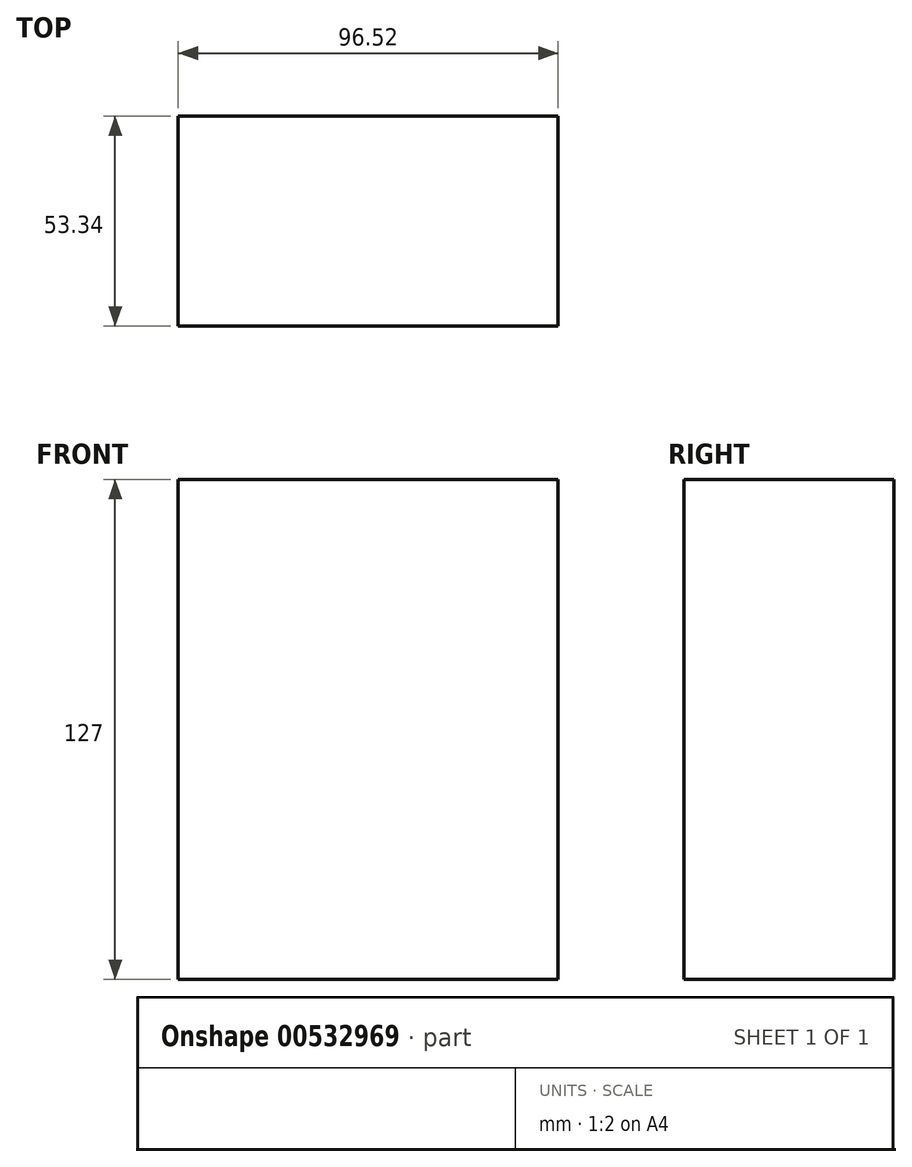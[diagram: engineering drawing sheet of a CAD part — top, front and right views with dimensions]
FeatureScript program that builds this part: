
annotation { "Feature Type Name" : "Feature", "Feature Type Description" : "" }
export const myFeature = defineFeature(function(context is Context, id is Id, definition is map)
    precondition{}
    {
        {
            var Q0;
            Q0=qCreatedBy(makeId("Front.planeOp"),FACE);
            var sketch = newSketch(context, id + "F0", { "sketchPlane" : qUnion([Q0])});
            skLineSegment(sketch, "E0.bottom", {"start": v(48.26, 63.5) * mm, "end": v(-48.26, 63.5) * mm});
            skLineSegment(sketch, "E0.top", {"start": v(48.26, -63.5) * mm, "end": v(-48.26, -63.5) * mm});
            skLineSegment(sketch, "E0.left", {"start": v(48.26, 63.5) * mm, "end": v(48.26, -63.5) * mm});
            skLineSegment(sketch, "E0.right", {"start": v(-48.26, 63.5) * mm, "end": v(-48.26, -63.5) * mm});
            skPoint(sketch, "E0.middle", {"position": v(0, 0) * mm});
            skSolve(sketch);
        }
        {
            var Q0;
            Q0 = qSketchRegion(id + "F0", true);
            extrude(context, id + "F1", {"entities" : qUnion([Q0]), "depth" : 53.34 * mm, "offsetDistance" : 25.4 * mm});
        }
    });
